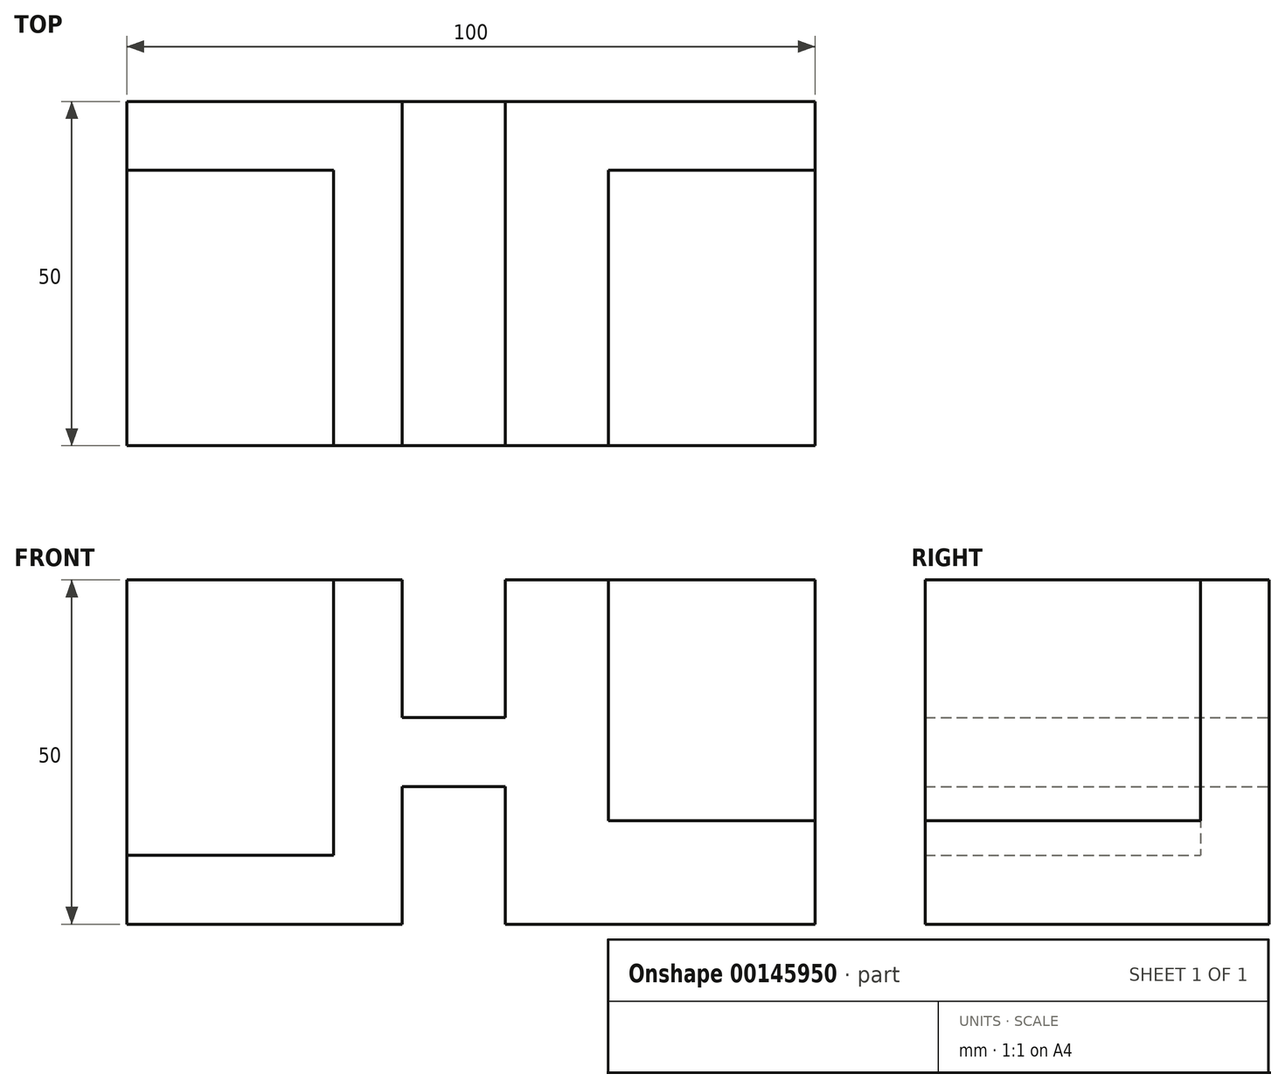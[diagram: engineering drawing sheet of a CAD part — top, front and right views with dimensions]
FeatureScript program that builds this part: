
annotation { "Feature Type Name" : "Feature", "Feature Type Description" : "" }
export const myFeature = defineFeature(function(context is Context, id is Id, definition is map)
    precondition{}
    {
        {
            var Q0;
            Q0=qCreatedBy(makeId("Front.planeOp"),FACE);
            var sketch = newSketch(context, id + "F0", { "sketchPlane" : qUnion([Q0])});
            skLineSegment(sketch, "E0", {"start": v(-17.5, 10) * mm, "end": v(-17.5, 50) * mm});
            skLineSegment(sketch, "E1", {"start": v(-7.5, 50) * mm, "end": v(-7.5, 30) * mm});
            skLineSegment(sketch, "E2", {"start": v(7.5, 50) * mm, "end": v(7.5, 30) * mm});
            skLineSegment(sketch, "E3", {"start": v(7.5, 30) * mm, "end": v(-7.5, 30) * mm});
            skLineSegment(sketch, "E4", {"start": v(-17.5, 50) * mm, "end": v(-7.5, 50) * mm});
            skLineSegment(sketch, "E5", {"start": v(7.5, 50) * mm, "end": v(22.5, 50) * mm});
            skLineSegment(sketch, "E6", {"start": v(-7.5, 20) * mm, "end": v(7.5, 20) * mm});
            skLineSegment(sketch, "E7", {"start": v(7.5, 20) * mm, "end": v(7.5, 0) * mm});
            skLineSegment(sketch, "E8", {"start": v(7.5, 0) * mm, "end": v(52.5, 0) * mm});
            skLineSegment(sketch, "E9", {"start": v(-7.5, 20) * mm, "end": v(-7.5, 0) * mm});
            skLineSegment(sketch, "E10", {"start": v(-7.5, 0) * mm, "end": v(-47.5, 0) * mm});
            skLineSegment(sketch, "E11", {"start": v(-47.5, 10) * mm, "end": v(-17.5, 10) * mm});
            skLineSegment(sketch, "E12", {"start": v(-47.5, 10) * mm, "end": v(-47.5, 0) * mm});
            skLineSegment(sketch, "E13", {"start": v(22.5, 50) * mm, "end": v(22.5, 15) * mm});
            skLineSegment(sketch, "E14", {"start": v(22.5, 15) * mm, "end": v(52.5, 15) * mm});
            skLineSegment(sketch, "E15", {"start": v(52.5, 15) * mm, "end": v(52.5, 0) * mm});
            skSolve(sketch);
        }
        {
            var Q0;
            Q0 = qSketchRegion(id + "F0", true);
            extrude(context, id + "F1", {"entities" : qUnion([Q0]), "depth" : 50 * mm});
        }
        {
            var Q0;
            Q0=qCreatedBy(makeId("Front.planeOp"),FACE);
            var sketch = newSketch(context, id + "F2", { "sketchPlane" : qUnion([Q0])});
            skPoint(sketch, "E16.0", {"position": v(-17.5, 50) * mm});
            skPoint(sketch, "E17.0", {"position": v(-47.5, 10) * mm});
            skLineSegment(sketch, "E18", {"start": v(-17.5, 50) * mm, "end": v(-47.5, 50) * mm});
            skLineSegment(sketch, "E19", {"start": v(-47.5, 50) * mm, "end": v(-47.5, 10) * mm});
            skLineSegment(sketch, "E20", {"start": v(-47.5, 10) * mm, "end": v(-17.5, 10) * mm});
            skLineSegment(sketch, "E21", {"start": v(-17.5, 10) * mm, "end": v(-17.5, 50) * mm});
            skPoint(sketch, "E22.0", {"position": v(22.5, 50) * mm});
            skPoint(sketch, "E23.0", {"position": v(52.5, 15) * mm});
            skLineSegment(sketch, "E24", {"start": v(22.5, 50) * mm, "end": v(22.5, 15) * mm});
            skLineSegment(sketch, "E25", {"start": v(22.5, 15) * mm, "end": v(52.5, 15) * mm});
            skLineSegment(sketch, "E26", {"start": v(22.5, 50) * mm, "end": v(52.5, 50) * mm});
            skLineSegment(sketch, "E27", {"start": v(52.5, 50) * mm, "end": v(52.5, 15) * mm});
            skSolve(sketch);
        }
        {
            var Q0;
            Q0 = qSketchRegion(id + "F2", true);
            extrude(context, id + "F3", {"entities" : qUnion([Q0]), "operationType" : NewBodyOperationType.ADD, "depth" : 10 * mm});
        }
    });
